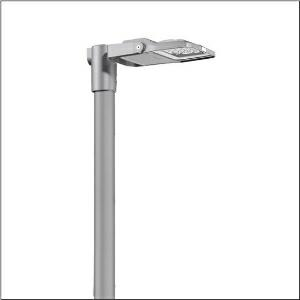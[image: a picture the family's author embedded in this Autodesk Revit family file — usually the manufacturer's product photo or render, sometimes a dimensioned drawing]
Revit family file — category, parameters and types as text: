
# Revit family: floodlight_fl_21_micro___pl64_5xa7761a2e3a_b0b9
name_source: partatom
category: Lighting Fixtures
units: mm (PartAtom-declared; Revit-internal decimal feet)

## family parameters
Cut with Voids When Loaded = No
Host = Face
Light Source = No
Part Type = Normal
Room Calculation Point = No
Round Connector Dimension = Use Diameter
Shared = No

## types (1)
- --- (1 x LED, 2870 lm, 23.1 W, 3000K)
    Apparent Load = 23 VA
    CIE Flux Codes = 28 80 98 100 100
    Color Rendering = 70
    Color Temperature = 3000K
    Default Elevation = 1800 mm
    Description = Floodlight FL 21 micro, floodlight, primary light control with lens, of PMMA, primary optical cover: protective disc, of toughened safety glass, transparent, light distribution: PL64, light emission: direct distribution, installation type: surface-mounted, LED, High Power LED, rated luminous flux: 2.870lm, luminous efficacy: 124lm/W, light colour: 730, colour temperature: 3000K, control gear: ECG iQ, control: optimised constant luminous flux control (CLO 2.0), Desk-Remote (wireless, voltage-free reading and setting of iQ features in the workshop via application-optimized NFC function/RFID function), Light-Fading, Smart-Wire, Night-Set, Lumen-Switch, Temp-Guard, Auto-Match, with terminal, 6-pole, mains connection: 220..240V, AC, 50/60Hz, start of lifetime: 23W, end of lifetime: 24W, reduction: 11W, luminaire housing, of diecast aluminium, powder-coated, Siteco® metallic grey (DB 702S), corrosivity category C5 according to DIN EN ISO 12944, mast bracket, of steel, galvanised, powder-coated, Siteco® metallic grey (DB 702S), protection rating (complete): IP66, insulation class (complete): insulation class II (safety insulation), certification: CE, protection symbol: D, impact resistance: IK07, permissible operating ambient temperature: -40..+40°C, permissible operating ambient temperature for outdoor applications: -40..+50°C, standard: DIN EN 12944, packaging unit: 1 piece

Light Distribution: PL64
    Height = 65 mm
    Lamp = 1 x LED
    Lamp Light Flux = 2870 lm
    Lamp Power = 23.1 W
    Lamp count = 1
    Length = 312 mm
    Luminous efficacy = 124 lm/W
    Manufacturer = Siteco
    ModVariant = No
    Model = 5XA7761A2E3A
    Number of Poles = 1
    OnlyDefault = Yes
    Power Factor = 1
    Product Name = Floodlight FL 21 micro | PL64
    Product group = floodlight | pylon top
    ProductGroupID = 6101
    Protection Class = Protection class II
    Protection Degree = IP 66
    RLX_Detail_Level = 1
    RlxData = <blob elided: 101561 chars, md5=5a9f43d3>
    Socket = socket
    Standby Power = 0 W
    System Light Flux = 2870 lm
    System Power = 23 W
    Type Comments = factory setting: luminous flux: 100 % | dim-lin: 254 | 455 mA
    Type Image = l_1007121.jpg
    URL = http://relux.com
    VarID = @adj_094419
    Voltage = 0 V
    Weight = 0.00 kg
    Width = 230 mm

## geometry (parser evidence)
native form markers: Blend x4, Sweep x12
no freeform markers — native parametric forms only
